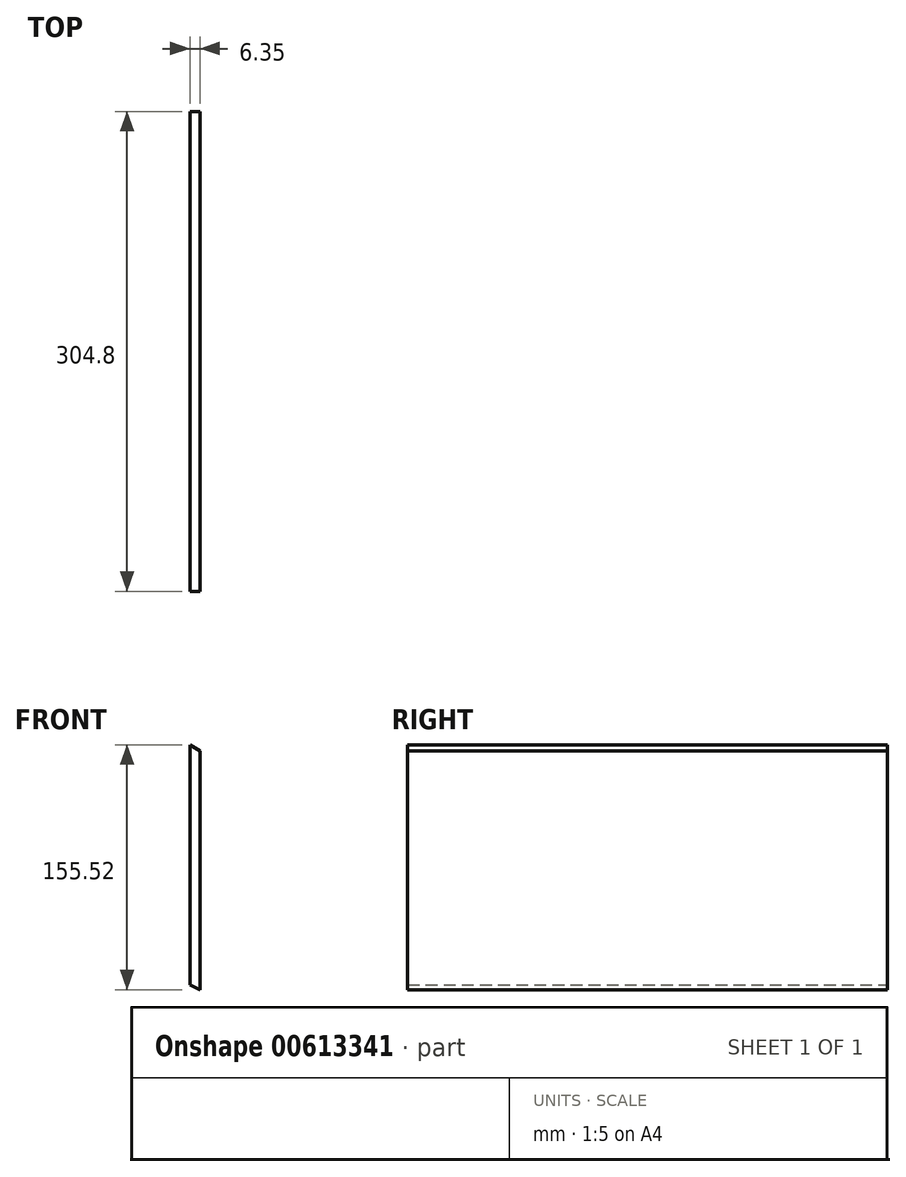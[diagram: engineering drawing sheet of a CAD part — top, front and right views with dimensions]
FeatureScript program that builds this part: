
annotation { "Feature Type Name" : "Feature", "Feature Type Description" : "" }
export const myFeature = defineFeature(function(context is Context, id is Id, definition is map)
    precondition{}
    {
        {
            var Q0;
            Q0=qCreatedBy(makeId("Front.planeOp"),FACE);
            var sketch = newSketch(context, id + "F0", { "sketchPlane" : qUnion([Q0])});
            skLineSegment(sketch, "E0.left", {"start": v(3.17, 72.28) * mm, "end": v(3.18, -79.32) * mm});
            skLineSegment(sketch, "E0.right", {"start": v(-3.18, 76.2) * mm, "end": v(-3.17, -76.2) * mm});
            skPoint(sketch, "E0.middle", {"position": v(0, 0) * mm});
            skLineSegment(sketch, "E1", {"start": v(-3.17, -76.2) * mm, "end": v(3.18, -79.32) * mm});
            skLineSegment(sketch, "E2", {"start": v(-3.18, 76.2) * mm, "end": v(3.17, 72.28) * mm});
            skPoint(sketch, "E3.orphan", {"position": v(3.17, 76.2) * mm});
            skPoint(sketch, "E0.top.start.orphan", {"position": v(3.18, -76.2) * mm});
            skSolve(sketch);
        }
        {
            var Q0;
            Q0 = qSketchRegion(id + "F0", true);
            extrude(context, id + "F1", {"entities" : qUnion([Q0]), "depth" : 304.8 * mm, "offsetDistance" : 25.4 * mm});
        }
    });
